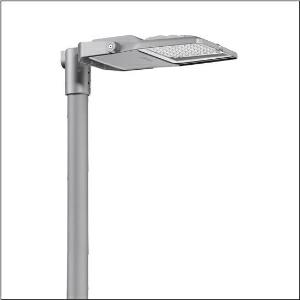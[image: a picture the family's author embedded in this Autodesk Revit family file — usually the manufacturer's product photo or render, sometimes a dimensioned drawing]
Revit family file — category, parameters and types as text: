
# Revit family: floodlight_fl_21_iq_mini___pl52_5xa7771b2d3a_cd8f
name_source: partatom
category: Lighting Fixtures
units: mm (PartAtom-declared; Revit-internal decimal feet)

## family parameters
Cut with Voids When Loaded = No
Host = Face
Light Source = No
Part Type = Normal
Room Calculation Point = No
Round Connector Dimension = Use Diameter
Shared = No

## types (1)
- --- (1 x LED, 6240 lm, 45.5 W, 3000K)
    Apparent Load = 46 VA
    CIE Flux Codes = 26 60 98 100 100
    Color Rendering = 70
    Color Temperature = 3000K
    Default Elevation = 1800 mm
    Description = Floodlight FL 21 iQ mini, floodlight, primary light control with lens, of PMMA, primary optical cover: protective disc, of toughened safety glass, transparent, light distribution: PL52, light emission: direct distribution, installation type: surface-mounted, LED, High Power LED, rated luminous flux: 6.240lm, luminous efficacy: 137lm/W, light colour: 730, colour temperature: 3000K, control: Auto-Match, Temp-Guard, Lumen-Switch, Night-Set, Smart-Wire, Light-Fading, Desk-Remote (wireless, voltage-free reading and setting of iQ features in the workshop via application-optimized NFC function/RFID function), optimised constant luminous flux control (CLO 2.0), with terminal, 6-pole, mains connection: 220..240V, AC, 50/60Hz, start of lifetime: 46W, end of service life: 48W, reduction: 22W, luminaire housing, of diecast aluminium, powder-coated, Siteco® metallic grey (DB 702S), corrosivity category C5 mid according to DIN EN ISO 12944, sealing non-destructively replaceable, please order mast flange separately, mast bracket, of steel, galvanised, powder-coated, Siteco® metallic grey (DB 702S), protection rating (complete): IP66, insulation class (complete): insulation class II (safety insulation), certification: CE, ENEC, VDE, protection symbol: D, impact resistance: IK08, permissible operating ambient temperature: -40..+40°C, permissible operating ambient temperature for outdoor applications: -40..+50°C, standard: DIN EN 12944, LABS conformity tested according to VDMA 24364:2018-05, packaging unit: 1 piece

Light Distribution: PL52
    Height = 70 mm
    Lamp = 1 x LED
    Lamp Light Flux = 6240 lm
    Lamp Power = 45.5 W
    Lamp count = 1
    Length = 485 mm
    Luminous efficacy = 137 lm/W
    Manufacturer = Siteco
    ModVariant = No
    Model = 5XA7771B2D3A
    Number of Poles = 1
    OnlyDefault = Yes
    Power Factor = 1
    Product Name = Floodlight FL 21 iQ mini | PL52
    Product group = floodlight | pylon annexe
    ProductGroupID = 6200
    Protection Class = Protection class II
    Protection Degree = IP 66
    RLX_Detail_Level = 1
    RLX_Emergency_Light_Flux = 0 lm
    RLX_Emergency_Type = 0
    RLX_Emergency_Type_DB = No
    RlxData = <blob elided: 101405 chars, md5=569a8ac0>
    Socket = socket
    Standby Power = 0 W
    System Light Flux = 6240 lm
    System Power = 46 W
    Type Comments = factory setting: luminous flux: 100 % | dim-lin: 254 | 463 mA
    Type Image = l_1007125.jpg
    URL = http://relux.com
    VarID = @adj_135429
    Voltage = 0 V
    Weight = 0.00 kg
    Width = 337 mm

## geometry (parser evidence)
native form markers: Blend x4, Sweep x13
no freeform markers — native parametric forms only
